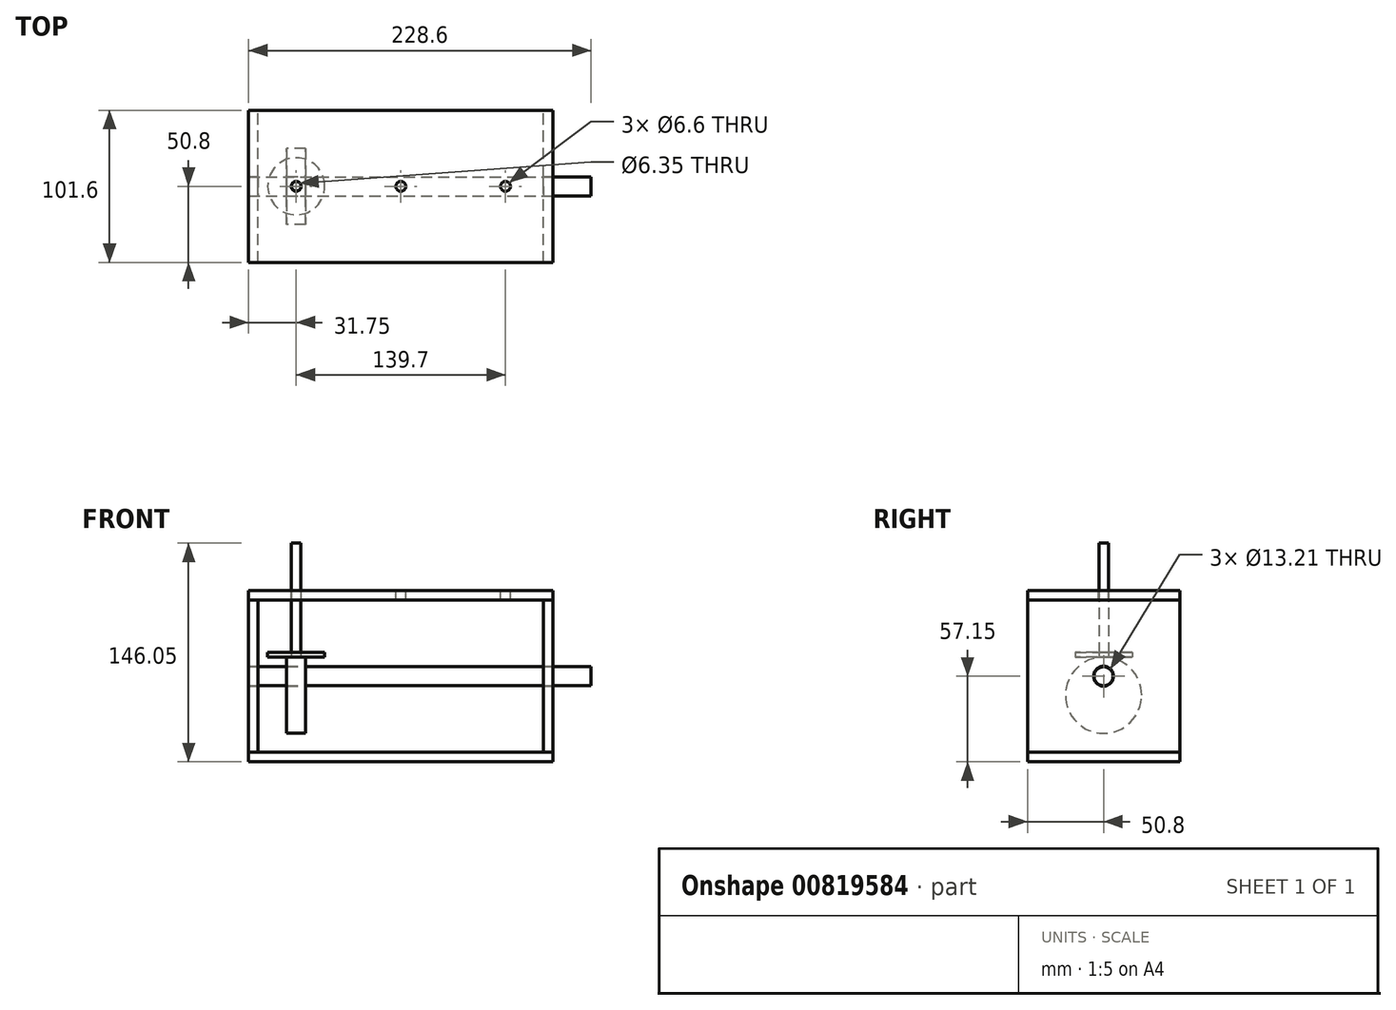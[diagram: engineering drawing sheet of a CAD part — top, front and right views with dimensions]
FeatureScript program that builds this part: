
annotation { "Feature Type Name" : "Feature", "Feature Type Description" : "" }
export const myFeature = defineFeature(function(context is Context, id is Id, definition is map)
    precondition{}
    {
        {
            assignVariable(context, id + "F0", {"name" : "depth", "anyValue" : 101.6 * mm});
        }
        {
            var Q0;
            Q0=qCreatedBy(makeId("Front.planeOp"),FACE);
            var sketch = newSketch(context, id + "F1", { "sketchPlane" : qUnion([Q0])});
            skLineSegment(sketch, "E0", {"start": v(-101.6, 0) * mm, "end": v(101.6, 0) * mm});
            skLineSegment(sketch, "E1", {"start": v(-101.6, 0) * mm, "end": v(-101.6, 114.3) * mm});
            skLineSegment(sketch, "E2", {"start": v(-101.6, 114.3) * mm, "end": v(101.6, 114.3) * mm});
            skLineSegment(sketch, "E3", {"start": v(101.6, 114.3) * mm, "end": v(101.6, 0) * mm});
            skLineSegment(sketch, "E4", {"start": v(-101.6, 107.95) * mm, "end": v(101.6, 107.95) * mm});
            skLineSegment(sketch, "E5", {"start": v(-101.6, 6.35) * mm, "end": v(101.6, 6.35) * mm});
            skLineSegment(sketch, "E6", {"start": v(-95.25, 6.35) * mm, "end": v(-95.25, 107.95) * mm});
            skLineSegment(sketch, "E7", {"start": v(95.25, 6.35) * mm, "end": v(95.25, 107.95) * mm});
            skLineSegment(sketch, "E8", {"start": v(101.6, 57.15) * mm, "end": v(95.25, 57.15) * mm, "construction": true});
            skLineSegment(sketch, "E9", {"start": v(-101.6, 57.15) * mm, "end": v(-95.25, 57.15) * mm, "construction": true});
            skLineSegment(sketch, "E10", {"start": v(0, 114.3) * mm, "end": v(0, 107.95) * mm, "construction": true});
            skLineSegment(sketch, "E11", {"start": v(0, 6.35) * mm, "end": v(0, 0) * mm, "construction": true});
            skLineSegment(sketch, "E12", {"start": v(-95.25, 57.15) * mm, "end": v(95.25, 57.15) * mm});
            skLineSegment(sketch, "E13.bottom", {"start": v(-76.2, 69.85) * mm, "end": v(-63.5, 69.85) * mm});
            skLineSegment(sketch, "E13.top", {"start": v(-76.2, 19.05) * mm, "end": v(-63.5, 19.05) * mm});
            skLineSegment(sketch, "E13.left", {"start": v(-76.2, 69.85) * mm, "end": v(-76.2, 19.05) * mm});
            skLineSegment(sketch, "E13.right", {"start": v(-63.5, 69.85) * mm, "end": v(-63.5, 19.05) * mm});
            skLineSegment(sketch, "E14.bottom", {"start": v(-6.35, 88.9) * mm, "end": v(6.35, 88.9) * mm});
            skLineSegment(sketch, "E14.top", {"start": v(-6.35, 38.1) * mm, "end": v(6.35, 38.1) * mm});
            skLineSegment(sketch, "E14.left", {"start": v(-6.35, 88.9) * mm, "end": v(-6.35, 38.1) * mm});
            skLineSegment(sketch, "E14.right", {"start": v(6.35, 88.9) * mm, "end": v(6.35, 38.1) * mm});
            skLineSegment(sketch, "E15.bottom", {"start": v(63.5, 88.9) * mm, "end": v(76.2, 88.9) * mm});
            skLineSegment(sketch, "E15.top", {"start": v(63.5, 38.1) * mm, "end": v(76.2, 38.1) * mm});
            skLineSegment(sketch, "E15.left", {"start": v(63.5, 88.9) * mm, "end": v(63.5, 38.1) * mm});
            skLineSegment(sketch, "E15.right", {"start": v(76.2, 88.9) * mm, "end": v(76.2, 38.1) * mm});
            skLineSegment(sketch, "E16", {"start": v(-6.35, 63.5) * mm, "end": v(6.35, 63.5) * mm});
            skLineSegment(sketch, "E17", {"start": v(63.5, 63.5) * mm, "end": v(76.2, 63.5) * mm});
            skLineSegment(sketch, "E18", {"start": v(-76.2, 44.45) * mm, "end": v(-63.5, 44.45) * mm});
            skLineSegment(sketch, "E19", {"start": v(-69.85, 44.45) * mm, "end": v(-69.85, 57.15) * mm, "construction": true});
            skLineSegment(sketch, "E20", {"start": v(0, 63.5) * mm, "end": v(0, 57.15) * mm, "construction": true});
            skLineSegment(sketch, "E21", {"start": v(69.85, 63.5) * mm, "end": v(69.85, 57.15) * mm, "construction": true});
            skLineSegment(sketch, "E22", {"start": v(-69.85, 69.85) * mm, "end": v(-69.85, 146.05) * mm, "construction": true});
            skLineSegment(sketch, "E23", {"start": v(0, 88.9) * mm, "end": v(0, 165.1) * mm, "construction": true});
            skLineSegment(sketch, "E24", {"start": v(69.85, 88.9) * mm, "end": v(69.85, 165.1) * mm, "construction": true});
            skSolve(sketch);
        }
        {
            var Q0;
            {var subQ1=sQuery(id+"F1.wireOp",EDGE,"E2");Q0=makeQuery(id+"F1.imprint","IMPRINT",FACE,{"disambiguationData":[TD([[makeQuery(id+"F1.imprint","IMPRINT",EDGE,{"derivedFrom":subQ1}),-1.0]])]});}
            var Q1;
            {var subQ1=sQuery(id+"F1.wireOp",EDGE,"E0");Q1=makeQuery(id+"F1.imprint","IMPRINT",FACE,{"disambiguationData":[TD([[makeQuery(id+"F1.imprint","IMPRINT",EDGE,{"derivedFrom":subQ1}),1.0]])]});}
            extrude(context, id + "F2", {"entities" : qUnion([Q0, Q1]), "endBound" : BoundingType.SYMMETRIC, "depth" : getVariable(context, 'depth'), "offsetDistance" : 25.4 * mm});
        }
        {
            var Q0;
            {var subQ5=sQuery(id+"F1.wireOp",EDGE,"E6");Q0=makeQuery(id+"F1.imprint","IMPRINT",FACE,{"disambiguationData":[TD([[makeQuery(id+"F1.imprint","IMPRINT",EDGE,{"derivedFrom":subQ5}),1.0]])]});}
            var Q1;
            {var subQ5=sQuery(id+"F1.wireOp",EDGE,"E7");Q1=makeQuery(id+"F1.imprint","IMPRINT",FACE,{"disambiguationData":[TD([[makeQuery(id+"F1.imprint","IMPRINT",EDGE,{"derivedFrom":subQ5}),-1.0]])]});}
            var Q2;
            Q2=makeQuery(id+"F2.opExtrude","CAP_FACE",FACE,{"disambiguationData":[OSD([sQuery(id+"F1.wireOp",EDGE,"E1"),sQuery(id+"F1.wireOp",EDGE,"E2"),sQuery(id+"F1.wireOp",EDGE,"E3"),sQuery(id+"F1.wireOp",EDGE,"E4")])],"isStart":false});
            var Q3;
            Q3=makeQuery(id+"F2.opExtrude","CAP_FACE",FACE,{"disambiguationData":[OSD([sQuery(id+"F1.wireOp",EDGE,"E1"),sQuery(id+"F1.wireOp",EDGE,"E2"),sQuery(id+"F1.wireOp",EDGE,"E3"),sQuery(id+"F1.wireOp",EDGE,"E4")])],"isStart":true});
            extrude(context, id + "F3", {"entities" : qUnion([Q0, Q1]), "endBound" : BoundingType.UP_TO_SURFACE, "depth" : 101.6 * mm, "endBoundEntityFace" : qUnion([Q2]), "offsetDistance" : 25.4 * mm, "hasSecondDirection" : true, "secondDirectionBound" : SecondDirectionBoundingType.UP_TO_SURFACE, "secondDirectionOppositeDirection" : true, "secondDirectionDepth" : 25.4 * mm, "secondDirectionBoundEntityFace" : qUnion([Q3])});
        }
        {
            var Q0;
            {var subQ0=sQuery(id+"F1.wireOp",EDGE,"E13.top");Q0=makeQuery(id+"F1.imprint","IMPRINT",FACE,{"disambiguationData":[TD([[makeQuery(id+"F1.imprint","IMPRINT",EDGE,{"derivedFrom":subQ0}),1.0]])]});}
            var Q1;
            Q1=sQuery(id+"F1.wireOp",EDGE,"E18");
            revolve(context, id + "F4", {"surfaceOperationType" : NewSurfaceOperationType.NEW, "entities" : qUnion([Q0]), "axis" : qUnion([Q1]), "revolveType" : RevolveType.FULL});
        }
        {
            var Q0;
            Q0=makeQuery(id+"F3.opExtrude","SWEPT_FACE",FACE,{"disambiguationData":[OSD([sQuery(id+"F1.wireOp",EDGE,"E3")])]});
            var sketch = newSketch(context, id + "F5", { "sketchPlane" : qUnion([Q0])});
            skCircle(sketch, "E25", {"center": v(0, 57.15) * mm, "radius": 6.35 * mm});
            skCircle(sketch, "E26", {"center": v(0, 57.15) * mm, "radius": 6.6 * mm});
            skSolve(sketch);
        }
        {
            var Q0;
            Q0=makeQuery(id+"F5.imprint","IMPRINT",FACE,{"disambiguationData":[TD([[makeQuery(id+"F5.imprint","IMPRINT",EDGE,{"derivedFrom":sQuery(id+"F5.wireOp",EDGE,"E25")}),1.0]])]});
            var Q1;
            Q1=makeQuery(id+"F5.imprint","IMPRINT",FACE,{"disambiguationData":[TD([[makeQuery(id+"F5.imprint","IMPRINT",EDGE,{"derivedFrom":sQuery(id+"F5.wireOp",EDGE,"E25")}),-1.0]])]});
            extrude(context, id + "F6", {"entities" : qUnion([Q0, Q1]), "operationType" : NewBodyOperationType.REMOVE, "endBound" : BoundingType.THROUGH_ALL, "oppositeDirection" : true, "depth" : 25.4 * mm, "offsetDistance" : 25.4 * mm});
        }
        {
            var Q0;
            Q0=makeQuery(id+"F5.imprint","IMPRINT",FACE,{"disambiguationData":[TD([[makeQuery(id+"F5.imprint","IMPRINT",EDGE,{"derivedFrom":sQuery(id+"F5.wireOp",EDGE,"E25")}),1.0]])]});
            var Q1;
            Q1=makeQuery(id+"F3.opExtrude","SWEPT_FACE",FACE,{"disambiguationData":[OSD([sQuery(id+"F1.wireOp",EDGE,"E1")])]});
            extrude(context, id + "F7", {"entities" : qUnion([Q0]), "endBound" : BoundingType.UP_TO_SURFACE, "oppositeDirection" : true, "depth" : 30.48 * mm, "endBoundEntityFace" : qUnion([Q1]), "offsetDistance" : 25.4 * mm, "hasSecondDirection" : true, "secondDirectionOppositeDirection" : false, "secondDirectionDepth" : 25.4 * mm});
        }
        {
            var Q0;
            Q0=makeQuery(id+"F7.opExtrude","SWEPT_BODY",BODY,{"disambiguationData":[OSD([sQuery(id+"F5.wireOp",EDGE,"E25")])]});
            var Q1;
            Q1=makeQuery(id+"F4.opRevolve","SWEPT_BODY",BODY,{"disambiguationData":[OSD([sQuery(id+"F1.wireOp",EDGE,"E13.top"),sQuery(id+"F1.wireOp",EDGE,"E13.left"),sQuery(id+"F1.wireOp",EDGE,"E13.right"),sQuery(id+"F1.wireOp",EDGE,"E18")])]});
            booleanBodies(context, id + "F8", {"operationType" : BooleanOperationType.SUBTRACTION, "tools" : qUnion([Q0]), "targets" : qUnion([Q1]), "keepTools" : true});
        }
        {
            var Q0;
            Q0=qCreatedBy(makeId("Top.planeOp"),FACE);
            var Q1;
            Q1=sQuery(id+"F1.wireOp",VERTEX,"E22.start");
            cPlane(context, id + "F9", {"entities" : qUnion([Q0, Q1]), "cplaneType" : CPlaneType.PLANE_POINT, "offset" : 25.4 * mm, "width" : 152.4 * mm, "height" : 152.4 * mm});
        }
        {
            var Q0;
            Q0=qCreatedBy(id+"F9.planeOp",FACE);
            var sketch = newSketch(context, id + "F10", { "sketchPlane" : qUnion([Q0])});
            skCircle(sketch, "E27", {"center": v(-69.85, 0) * mm, "radius": 3.18 * mm});
            skCircle(sketch, "E28", {"center": v(-69.85, 0) * mm, "radius": 19.05 * mm});
            skSolve(sketch);
        }
        {
            var Q0;
            Q0=makeQuery(id+"F2.opExtrude","SWEPT_FACE",FACE,{"disambiguationData":[OSD([sQuery(id+"F1.wireOp",EDGE,"E2")])]});
            var sketch = newSketch(context, id + "F11", { "sketchPlane" : qUnion([Q0])});
            skPoint(sketch, "E29", {"position": v(-69.85, 0) * mm});
            skPoint(sketch, "E30", {"position": v(0, 0) * mm});
            skPoint(sketch, "E31", {"position": v(69.85, 0) * mm});
            skSolve(sketch);
        }
        {
            var Q0;
            Q0=sQuery(id+"F11.wireOp",VERTEX,"E29");
            var Q1;
            Q1=sQuery(id+"F11.wireOp",VERTEX,"E30");
            var Q2;
            Q2=sQuery(id+"F11.wireOp",VERTEX,"E31");
            var Q3;
            Q3=makeQuery(id+"F2.opExtrude","SWEPT_BODY",BODY,{"disambiguationData":[OSD([sQuery(id+"F1.wireOp",EDGE,"E1"),sQuery(id+"F1.wireOp",EDGE,"E2"),sQuery(id+"F1.wireOp",EDGE,"E3"),sQuery(id+"F1.wireOp",EDGE,"E4")])]});
            hole(context, id + "F12", {"style" : HoleStyle.SIMPLE, "endStyle" : HoleEndStyle.THROUGH, "holeDiameter" : 6.6 * mm, "majorDiameter" : 6.35 * mm, "isTappedThrough" : true, "tappedDepth" : 12.7 * mm, "tapClearance" : 3, "locations" : qUnion([Q0, Q1, Q2]), "scope" : qUnion([Q3])});
        }
        {
            var Q0;
            Q0=makeQuery(id+"F10.imprint","IMPRINT",FACE,{"disambiguationData":[TD([[makeQuery(id+"F10.imprint","IMPRINT",EDGE,{"derivedFrom":sQuery(id+"F10.wireOp",EDGE,"E27")}),1.0]])]});
            var Q1;
            Q1=sQuery(id+"F1.wireOp",VERTEX,"E22.end");
            extrude(context, id + "F13", {"entities" : qUnion([Q0]), "endBound" : BoundingType.UP_TO_VERTEX, "depth" : 25.4 * mm, "endBoundEntityVertex" : qUnion([Q1]), "offsetDistance" : 25.4 * mm});
        }
        {
            var Q0;
            Q0=makeQuery(id+"F10.imprint","IMPRINT",FACE,{"disambiguationData":[TD([[makeQuery(id+"F10.imprint","IMPRINT",EDGE,{"derivedFrom":sQuery(id+"F10.wireOp",EDGE,"E27")}),-1.0]])]});
            extrude(context, id + "F14", {"entities" : qUnion([Q0]), "depth" : 3.17 * mm, "offsetDistance" : 25.4 * mm});
        }
    });
